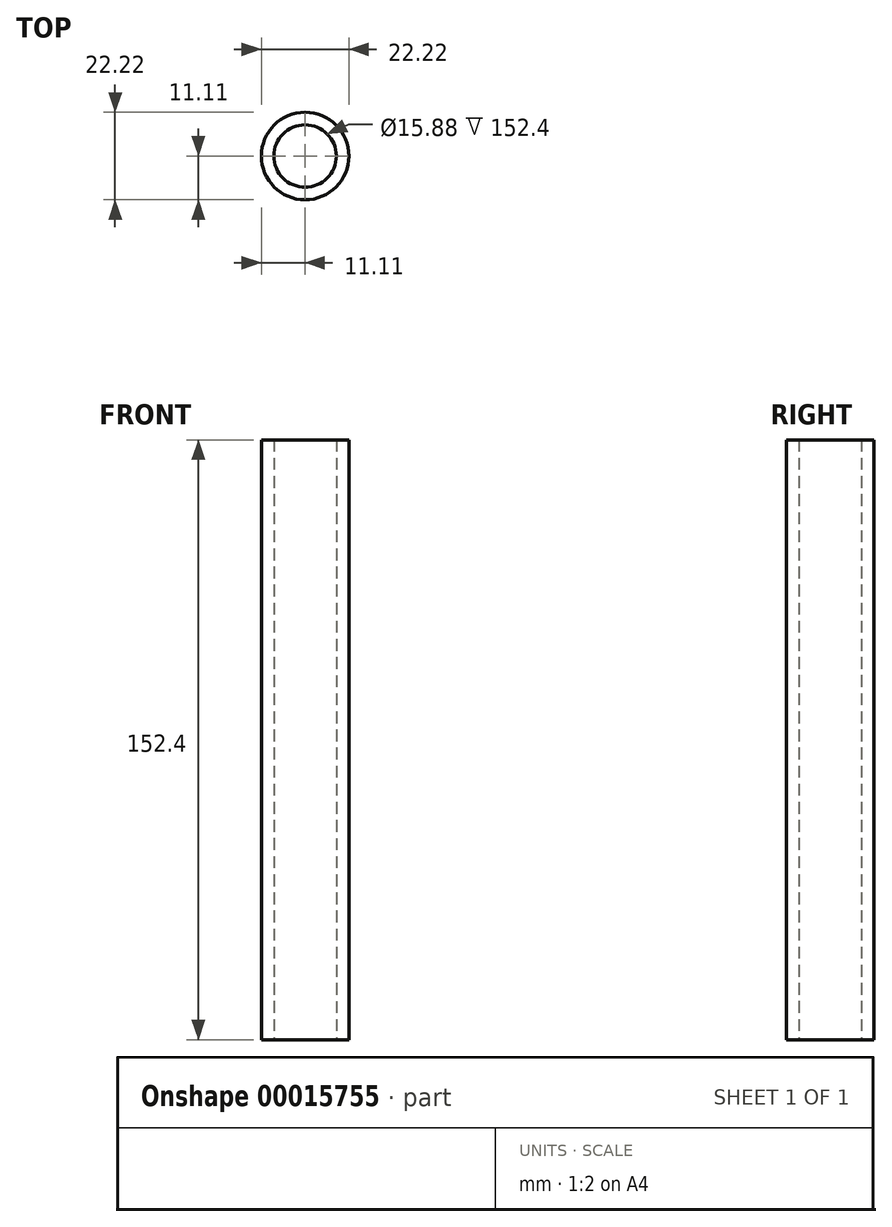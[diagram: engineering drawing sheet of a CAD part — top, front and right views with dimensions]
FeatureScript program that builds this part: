
annotation { "Feature Type Name" : "Feature", "Feature Type Description" : "" }
export const myFeature = defineFeature(function(context is Context, id is Id, definition is map)
    precondition{}
    {
        {
            var Q0;
            Q0=qCreatedBy(makeId("Top.planeOp"),FACE);
            var sketch = newSketch(context, id + "F0", { "sketchPlane" : qUnion([Q0])});
            skCircle(sketch, "E0", {"center": v(0, 0) * mm, "radius": 11.11 * mm});
            skCircle(sketch, "E1", {"center": v(0, 0) * mm, "radius": 7.94 * mm});
            skSolve(sketch);
        }
        {
            var Q0;
            Q0 = qSketchRegion(id + "F0", true);
            extrude(context, id + "F1", {"entities" : qUnion([Q0]), "depth" : 152.4 * mm});
        }
    });
